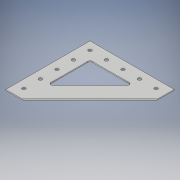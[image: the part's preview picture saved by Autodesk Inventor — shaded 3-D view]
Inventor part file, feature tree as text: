
AUTODESK INVENTOR PART (.ipt)
format: ipt  version: 2018 (Build 220112000, 112)  size: 172,544 bytes
history: native  units: in
note: dims shown in document units (in); Inventor stores cm internally (conversion verified against a paired STEP export)
features: sketch x4, extrude x3, hole x1, fillet x1
ambient origin geometry x8: Origin, YZ Plane, XZ Plane, XY Plane, X Axis, Y Axis, Z Axis, Center Point
bodies: Solid1 (feature_tree)
feature tree (9):
  extrude  "Extrusion1"  Depth=6.0in
  hole  "Hole1"  [1 undecoded]
  extrude  "Extrusion2"  Depth=0.0625in TaperAngle=0.0deg
  extrude  "Extrusion3"  Depth=1.0in
  fillet  "Fillet1"  Radius=1.0in
  sketch  "Sketch1"  dims[d0=1.0in d1=6.0in]
  sketch  "Sketch2"  dims[d2=6.0in d3=1.0in]
  sketch  "Sketch3"  dims[d4=1.0in d5=0.0625in d6=0.0in]
  sketch  "Sketch4"  dims[d7=1.0in d8=1.0in d9=1.0in d10=1.0in d11=1.0in d12=1.0in d13=1.0in d14=1.0in d15=1.0in d16=1.0in d17=0.2in d18=0.2in d19=0.2in d20=0.2in d21=0.2in d22=0.2in d23=0.2in d24=0.2in d25=0.2in d26=0.75in d27=0.375in d28=0.25in d29=0.5635in d30=1.0in d31=0.8108in d32=0.5in d33=0.5in d34=0.0625in d35=0.0in d36=1.0in d37=0.0625in d38=0.0in d39=0.125in]
note: 1 required parameter value undecoded (feature->parameter linkage not recoverable at this tier; creation-order binding heuristic only, values carry confidence <= 0.55)
